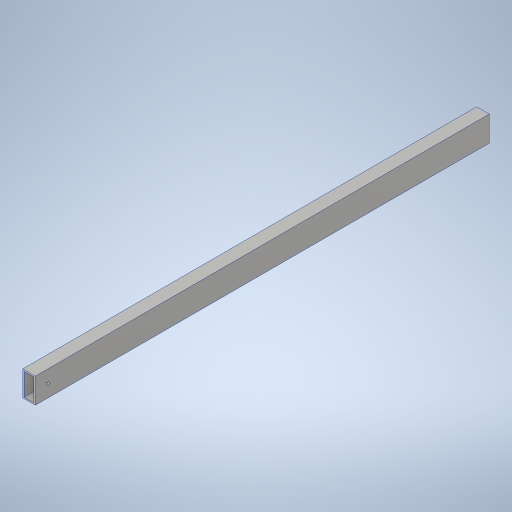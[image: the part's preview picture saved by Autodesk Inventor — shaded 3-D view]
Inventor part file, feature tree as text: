
AUTODESK INVENTOR PART (.ipt)
format: ipt  version: 2023.4 (Build 274418000, 418)  size: 256,512 bytes
history: native  units: in
note: dims shown in document units (in); Inventor stores cm internally (conversion verified against a paired STEP export)
features: extrude x1, hole x1, sketch x1
ambient origin geometry x8: Origin, YZ Plane, XZ Plane, XY Plane, X Axis, Y Axis, Z Axis, Center Point
bodies: Solid1 (feature_tree)
feature tree (3):
  extrude  "Extrusion1"  Depth=1.0in
  hole  "Hole1"  [1 undecoded]
  sketch  "Sketch2"  dims[d4=0.0in d5=1.0in d6=0.201in d7=0.75in d8=0.385in d9=0.25in d10=0.5635in d11=1.0in d12=0.8108in]
note: 1 required parameter value undecoded (feature->parameter linkage not recoverable at this tier; creation-order binding heuristic only, values carry confidence <= 0.55)
